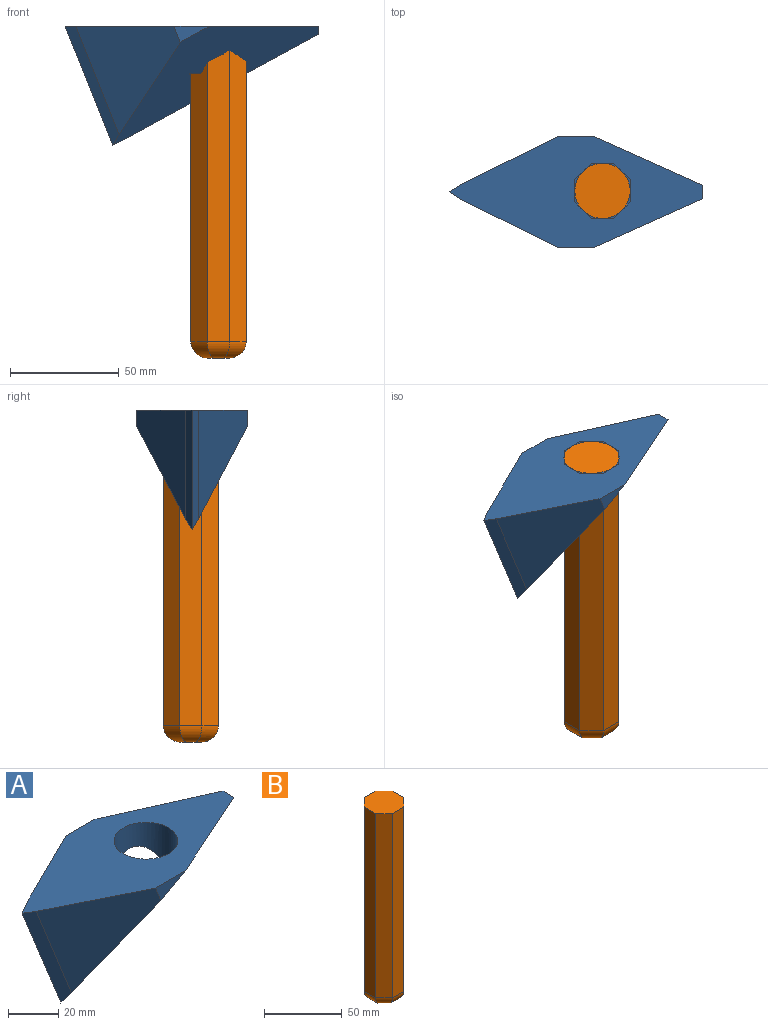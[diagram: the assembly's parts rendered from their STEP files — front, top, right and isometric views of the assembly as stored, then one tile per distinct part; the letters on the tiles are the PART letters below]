
ASSEMBLY  parts=2 mates=1
PART A: 14 faces, bbox 116.4x50.8x54.8 mm
  f0: plane 23.07x12.29mm, normal (1,0,0.04), area 150.7mm2, adj f1,f10,f11,f12
  f1: plane 23.07x5.04mm, normal (0,0,-1), area 42.3mm2, adj f0,f10,f11,f13
  f2: plane 6.18x3.73mm, normal (1,0,0), area 11.5mm2, adj f3,f10,f11
  f3: plane 116.44x50.8mm, normal (0,0,1), area 3053.6mm2, adj f2,f4,f5,f6,f7,f8,f9,f10
  f4: plane 16.59x7.37mm, normal (0,-1,0), area 61.1mm2, adj f3,f9,f10
  f5: plane 16.59x7.37mm, normal (0,1,0), area 61.1mm2, adj f3,f8,f11
  f6: plane 54.82x24.73mm, normal (-0.52,-0.83,-0.21), area 308.5mm2, adj f3,f7,f9,f10
  f7: plane 54.82x24.73mm, normal (-0.52,0.83,-0.21), area 308.5mm2, adj f3,f6,f8,f11
  f8: plane 49.61x47.98mm, normal (-0.44,0.88,-0.17), area 1454.7mm2, adj f3,f5,f7,f11
  f9: plane 49.61x47.98mm, normal (-0.44,-0.88,-0.17), area 1454.7mm2, adj f3,f4,f6,f10
  f10: plane 94.54x54.83mm, normal (0.33,-0.73,-0.6), area 1994.3mm2, adj f0,f1,f2,f3,f4,f6,f9,f11
  f11: plane 94.53x54.82mm, normal (0.33,0.73,-0.6), area 1957.5mm2, adj f0,f1,f2,f3,f5,f7,f8,f10
  f12: cylinder r=12.7mm len=3.93mm, axis (0,0,-1), area 6.7mm2, adj f0,f10,f11
  f13: cylinder r=12.7mm len=25.4mm, axis (0,0,-1), area 1357mm2, adj f1,f3,f10,f11
PART B: 18 faces, bbox 25.4x25.4x152.4 mm
  f0: plane 144.78x10.16mm, normal (0,1,0), area 1471mm2, adj f4,f7,f9,f12
  f1: plane 144.78x10.16mm, normal (-1,0,0), area 1471mm2, adj f4,f6,f7,f16
  f2: plane 144.78x10.16mm, normal (0,-1,0), area 1471mm2, adj f4,f6,f8,f15
  f3: plane 144.78x10.16mm, normal (1,0,0), area 1471mm2, adj f4,f8,f9,f11
  f4: plane 25.4x25.4mm, normal (0,0,1), area 529mm2, adj f0,f1,f2,f3,f6,f7,f8,f9
  f5: plane 10.16x10.16mm, normal (0,0,-1), area 83.3mm2, adj f10,f11,f12,f13,f14,f15,f16,f17
  f6: plane 144.78x7.62mm, normal (-0.71,-0.71,0), area 1560.2mm2, adj f1,f2,f4,f17
  f7: plane 144.78x7.62mm, normal (-0.71,0.71,0), area 1560.2mm2, adj f0,f1,f4,f14
  f8: plane 144.78x7.62mm, normal (0.71,-0.71,0), area 1560.2mm2, adj f2,f3,f4,f13
  f9: plane 144.78x7.62mm, normal (0.71,0.71,0), area 1560.2mm2, adj f0,f3,f4,f10
  f10: cylinder r=7.62mm len=13.01mm, axis (0.71,-0.71,0), area 101.5mm2, adj f5,f9,f11,f12
  f11: cylinder r=7.62mm len=10.16mm, axis (0,1,0), area 94.2mm2, adj f3,f5,f10,f13
  f12: cylinder r=7.62mm len=10.16mm, axis (-1,0,0), area 94.2mm2, adj f0,f5,f10,f14
  f13: cylinder r=7.62mm len=13.01mm, axis (0.71,0.71,0), area 101.5mm2, adj f5,f8,f11,f15
  f14: cylinder r=7.62mm len=13.01mm, axis (-0.71,-0.71,0), area 101.5mm2, adj f5,f7,f12,f16
  f15: cylinder r=7.62mm len=10.16mm, axis (1,0,0), area 94.2mm2, adj f2,f5,f13,f17
  f16: cylinder r=7.62mm len=10.16mm, axis (0,-1,0), area 94.2mm2, adj f1,f5,f14,f17
  f17: cylinder r=7.62mm len=13.01mm, axis (-0.71,0.71,0), area 101.5mm2, adj f5,f6,f15,f16
PLACE A t=(-14.68,30.97,-144.46)mm
PLACE B t=(-26.28,-6.68,-245.79)mm
MATE pin_slot B.f4 <-> A.f12  axis (0,0,1) through (-14.68,6.09,-93.39)mm
